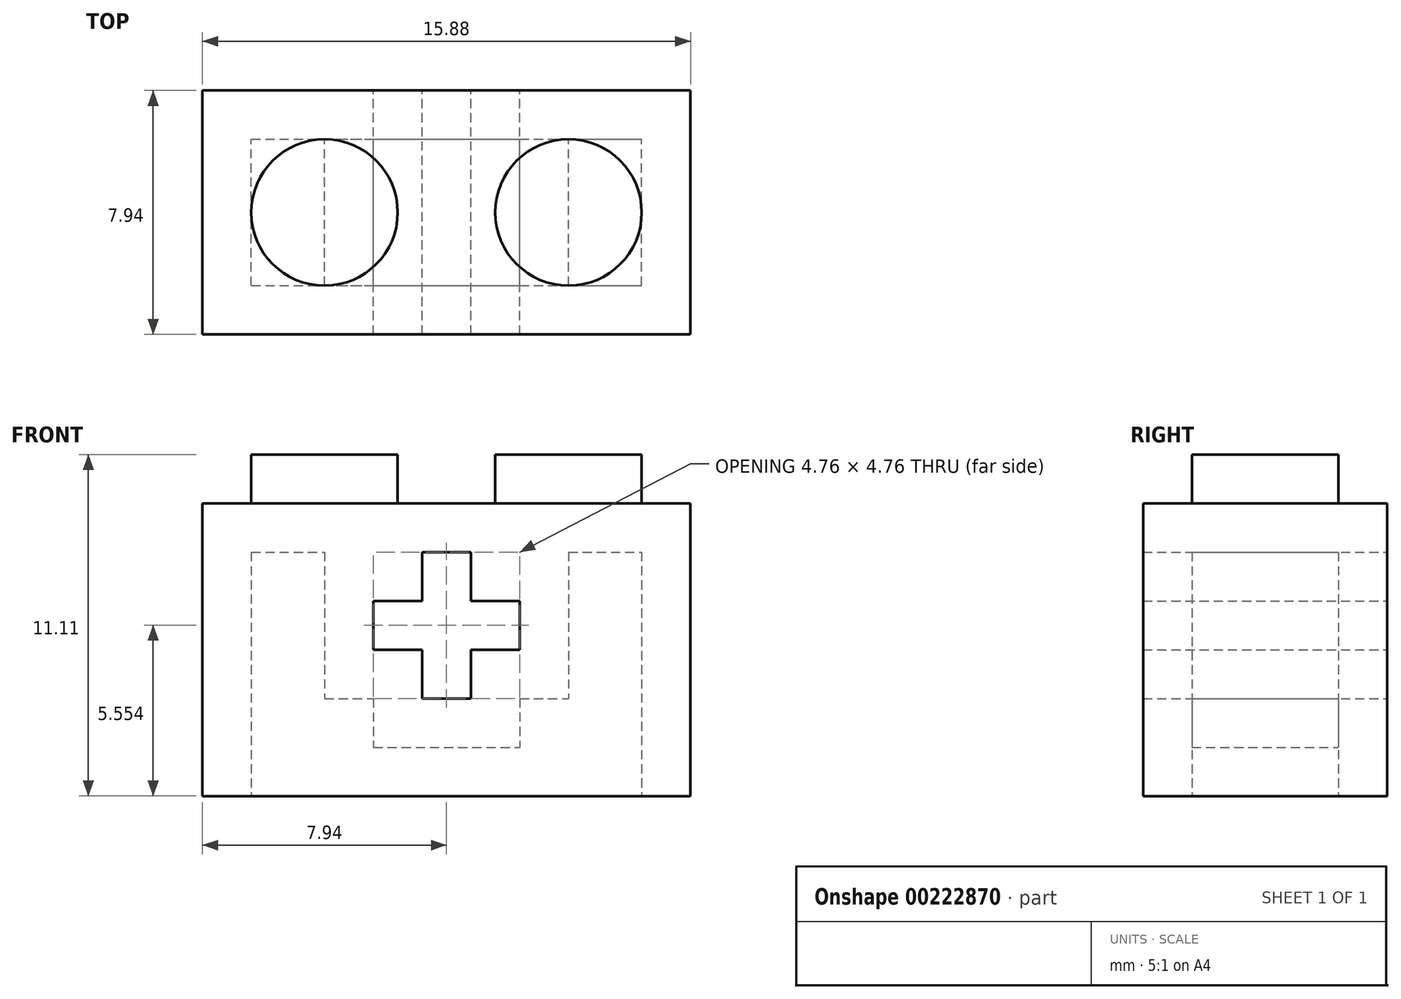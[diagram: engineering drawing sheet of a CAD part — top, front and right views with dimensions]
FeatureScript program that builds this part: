
annotation { "Feature Type Name" : "Feature", "Feature Type Description" : "" }
export const myFeature = defineFeature(function(context is Context, id is Id, definition is map)
    precondition{}
    {
        {
            var Q0;
            Q0=qCreatedBy(makeId("Front.planeOp"),FACE);
            var sketch = newSketch(context, id + "F0", { "sketchPlane" : qUnion([Q0])});
            skLineSegment(sketch, "E0.bottom", {"start": v(-7.94, 4.76) * mm, "end": v(7.94, 4.76) * mm});
            skLineSegment(sketch, "E0.top", {"start": v(-7.94, -4.76) * mm, "end": v(7.94, -4.76) * mm});
            skLineSegment(sketch, "E0.left", {"start": v(-7.94, 4.76) * mm, "end": v(-7.94, -4.76) * mm});
            skLineSegment(sketch, "E0.right", {"start": v(7.94, 4.76) * mm, "end": v(7.94, -4.76) * mm});
            skLineSegment(sketch, "E1.bottom", {"start": v(-0.8, 3.17) * mm, "end": v(0.8, 3.17) * mm});
            skLineSegment(sketch, "E1.top", {"start": v(-0.8, -1.59) * mm, "end": v(0.8, -1.59) * mm});
            skLineSegment(sketch, "E1.left", {"start": v(-0.8, 3.17) * mm, "end": v(-0.8, -1.59) * mm});
            skLineSegment(sketch, "E1.right", {"start": v(0.8, 3.17) * mm, "end": v(0.8, -1.59) * mm});
            skPoint(sketch, "E1.middle", {"position": v(0, 0) * mm});
            skLineSegment(sketch, "E2.bottom", {"start": v(-2.38, 1.59) * mm, "end": v(2.38, 1.59) * mm});
            skLineSegment(sketch, "E2.top", {"start": v(-2.38, 0) * mm, "end": v(2.38, 0) * mm});
            skLineSegment(sketch, "E2.left", {"start": v(-2.38, 1.59) * mm, "end": v(-2.38, 0) * mm});
            skLineSegment(sketch, "E2.right", {"start": v(2.38, 1.59) * mm, "end": v(2.38, 0) * mm});
            skLineSegment(sketch, "E3", {"start": v(-0.8, 3.17) * mm, "end": v(0.8, -1.59) * mm});
            skLineSegment(sketch, "E4", {"start": v(-2.38, 0) * mm, "end": v(2.38, 1.59) * mm});
            skSolve(sketch);
        }
        {
            var Q0;
            Q0 = qSketchRegion(id + "F0", true);
            extrude(context, id + "F1", {"entities" : qUnion([Q0]), "depth" : 7.94 * mm});
        }
        {
            var Q0;
            Q0=makeQuery(id+"F1.opExtrude","SWEPT_FACE",FACE,{"disambiguationData":[OSD([sQuery(id+"F0.wireOp",EDGE,"E0.top")])]});
            shell(context, id + "F2", {"entities" : qUnion([Q0]), "thickness" : 1.59 * mm});
        }
        {
            var Q0;
            Q0=makeQuery(id+"F1.opExtrude","SWEPT_FACE",FACE,{"disambiguationData":[OSD([sQuery(id+"F0.wireOp",EDGE,"E0.bottom")])]});
            var sketch = newSketch(context, id + "F3", { "sketchPlane" : qUnion([Q0])});
            skCircle(sketch, "E5", {"center": v(-3.97, -3.97) * mm, "radius": 2.38 * mm});
            skCircle(sketch, "E6.1.0.0", {"center": v(3.97, -3.97) * mm, "radius": 2.38 * mm});
            skLineSegment(sketch, "E6.direction1", {"start": v(-3.97, -3.97) * mm, "end": v(3.97, -3.97) * mm, "construction": true});
            skSolve(sketch);
        }
        {
            var Q0;
            Q0 = qSketchRegion(id + "F3", true);
            extrude(context, id + "F4", {"entities" : qUnion([Q0]), "operationType" : NewBodyOperationType.ADD, "depth" : 1.59 * mm});
        }
    });
